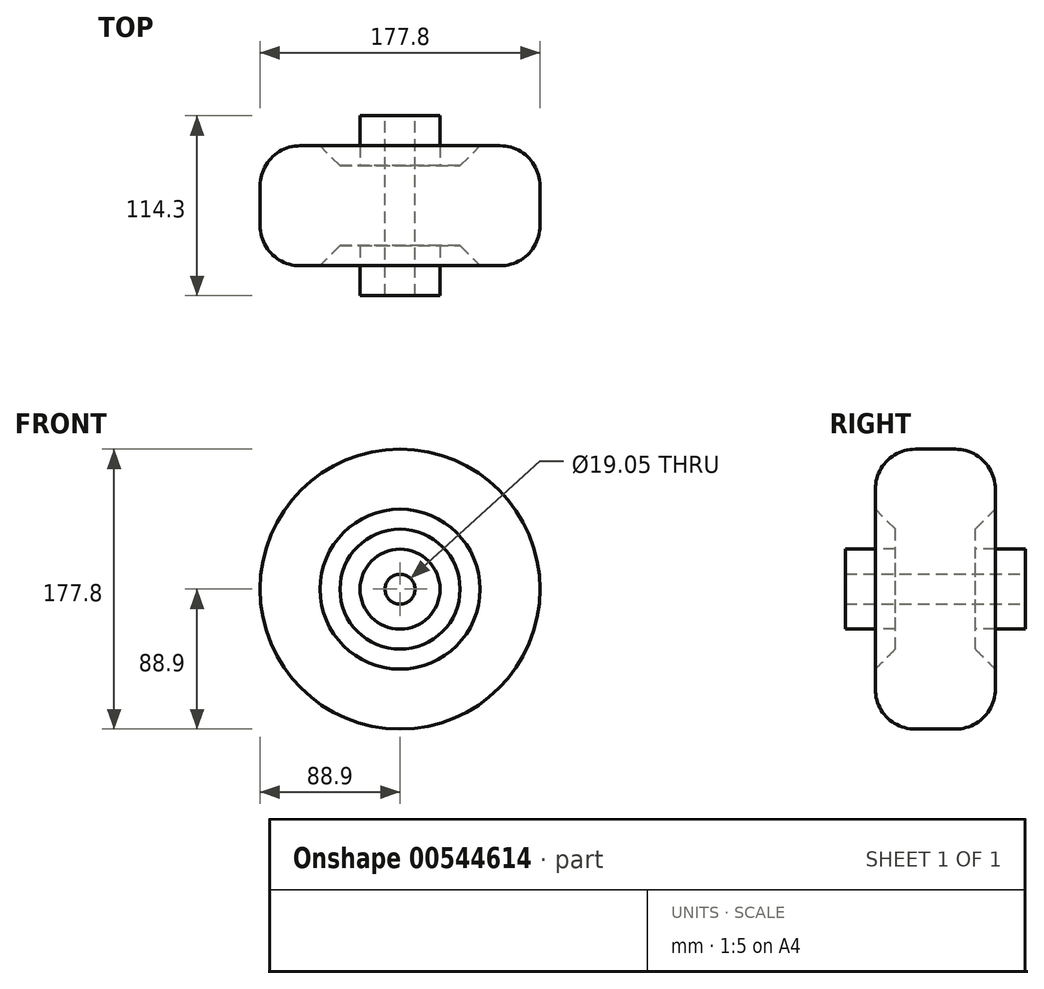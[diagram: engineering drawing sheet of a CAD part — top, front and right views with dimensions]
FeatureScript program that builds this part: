
annotation { "Feature Type Name" : "Feature", "Feature Type Description" : "" }
export const myFeature = defineFeature(function(context is Context, id is Id, definition is map)
    precondition{}
    {
        {
            var Q0;
            Q0=qCreatedBy(makeId("Right.planeOp"),FACE);
            var sketch = newSketch(context, id + "F0", { "sketchPlane" : qUnion([Q0])});
            skLineSegment(sketch, "E0", {"start": v(0, 0) * mm, "end": v(154.05, 0) * mm, "construction": true});
            skLineSegment(sketch, "E1", {"start": v(0, 0) * mm, "end": v(0, 25.4) * mm});
            skLineSegment(sketch, "E2", {"start": v(0, 25.4) * mm, "end": v(0, 25.4) * mm});
            skLineSegment(sketch, "E3", {"start": v(0, 25.4) * mm, "end": v(31.75, 25.4) * mm});
            skLineSegment(sketch, "E4", {"start": v(31.75, 25.4) * mm, "end": v(31.75, 38.1) * mm});
            skLineSegment(sketch, "E5", {"start": v(31.75, 38.1) * mm, "end": v(19.05, 50.8) * mm});
            skLineSegment(sketch, "E6", {"start": v(19.05, 50.8) * mm, "end": v(19.05, 88.9) * mm});
            skLineSegment(sketch, "E7", {"start": v(19.05, 88.9) * mm, "end": v(95.25, 88.9) * mm});
            skLineSegment(sketch, "E8", {"start": v(95.25, 88.9) * mm, "end": v(95.25, 50.8) * mm});
            skLineSegment(sketch, "E9", {"start": v(82.55, 25.4) * mm, "end": v(82.55, 38.1) * mm});
            skLineSegment(sketch, "E10", {"start": v(82.55, 38.1) * mm, "end": v(95.25, 50.8) * mm});
            skLineSegment(sketch, "E11", {"start": v(82.55, 25.4) * mm, "end": v(114.3, 25.4) * mm});
            skLineSegment(sketch, "E12", {"start": v(114.3, 25.4) * mm, "end": v(114.3, 0) * mm});
            skLineSegment(sketch, "E13", {"start": v(114.3, 0) * mm, "end": v(0, 0) * mm});
            skSolve(sketch);
        }
        {
            var Q0;
            Q0=makeQuery(id+"F0.imprint","IMPRINT",FACE,{"disambiguationData":[TD([[makeQuery(id+"F0.imprint","IMPRINT",EDGE,{"derivedFrom":sQuery(id+"F0.wireOp",EDGE,"E1")}),-1.0]])]});
            var Q1;
            Q1=sQuery(id+"F0.wireOp",EDGE,"E0");
            revolve(context, id + "F1", {"entities" : qUnion([Q0]), "axis" : qUnion([Q1]), "revolveType" : RevolveType.FULL});
        }
        {
            var Q0;
            Q0=makeQuery(id+"F1.opRevolve","SWEPT_FACE",FACE,{"disambiguationData":[OSD([sQuery(id+"F0.wireOp",EDGE,"E12")])]});
            var sketch = newSketch(context, id + "F2", { "sketchPlane" : qUnion([Q0])});
            skPoint(sketch, "E14", {"position": v(0, 0) * mm});
            skSolve(sketch);
        }
        {
            var Q0;
            Q0=sQuery(id+"F2.wireOp",VERTEX,"E14");
            var Q1;
            Q1=makeQuery(id+"F1.opRevolve","SWEPT_BODY",BODY,{"disambiguationData":[OSD([sQuery(id+"F0.wireOp",EDGE,"E1"),sQuery(id+"F0.wireOp",EDGE,"E3"),sQuery(id+"F0.wireOp",EDGE,"E4"),sQuery(id+"F0.wireOp",EDGE,"E5"),sQuery(id+"F0.wireOp",EDGE,"E6"),sQuery(id+"F0.wireOp",EDGE,"E7"),sQuery(id+"F0.wireOp",EDGE,"E8"),sQuery(id+"F0.wireOp",EDGE,"E9"),sQuery(id+"F0.wireOp",EDGE,"E10"),sQuery(id+"F0.wireOp",EDGE,"E11"),sQuery(id+"F0.wireOp",EDGE,"E12"),sQuery(id+"F0.wireOp",EDGE,"E13")])]});
            hole(context, id + "F3", {"style" : HoleStyle.SIMPLE, "endStyle" : HoleEndStyle.THROUGH, "holeDiameter" : 19.05 * mm, "majorDiameter" : 6.35 * mm, "isTappedThrough" : true, "tappedDepth" : 12.7 * mm, "tapClearance" : 3, "locations" : qUnion([Q0]), "scope" : qUnion([Q1])});
        }
        {
            var Q0;
            Q0=makeQuery(id+"F1.opRevolve","SWEPT_EDGE",EDGE,{"disambiguationData":[OSD([sQuery(id+"F0.wireOp",EDGE,"E7"),sQuery(id+"F0.wireOp",EDGE,"E8")])]});
            var Q1;
            Q1=makeQuery(id+"F1.opRevolve","SWEPT_EDGE",EDGE,{"disambiguationData":[OSD([sQuery(id+"F0.wireOp",EDGE,"E6"),sQuery(id+"F0.wireOp",EDGE,"E7")])]});
            fillet(context, id + "F4", {"entities" : qUnion([Q0, Q1]), "radius" : 25.4 * mm, "tangentPropagation" : true, "allowEdgeOverflow" : false});
        }
    });
